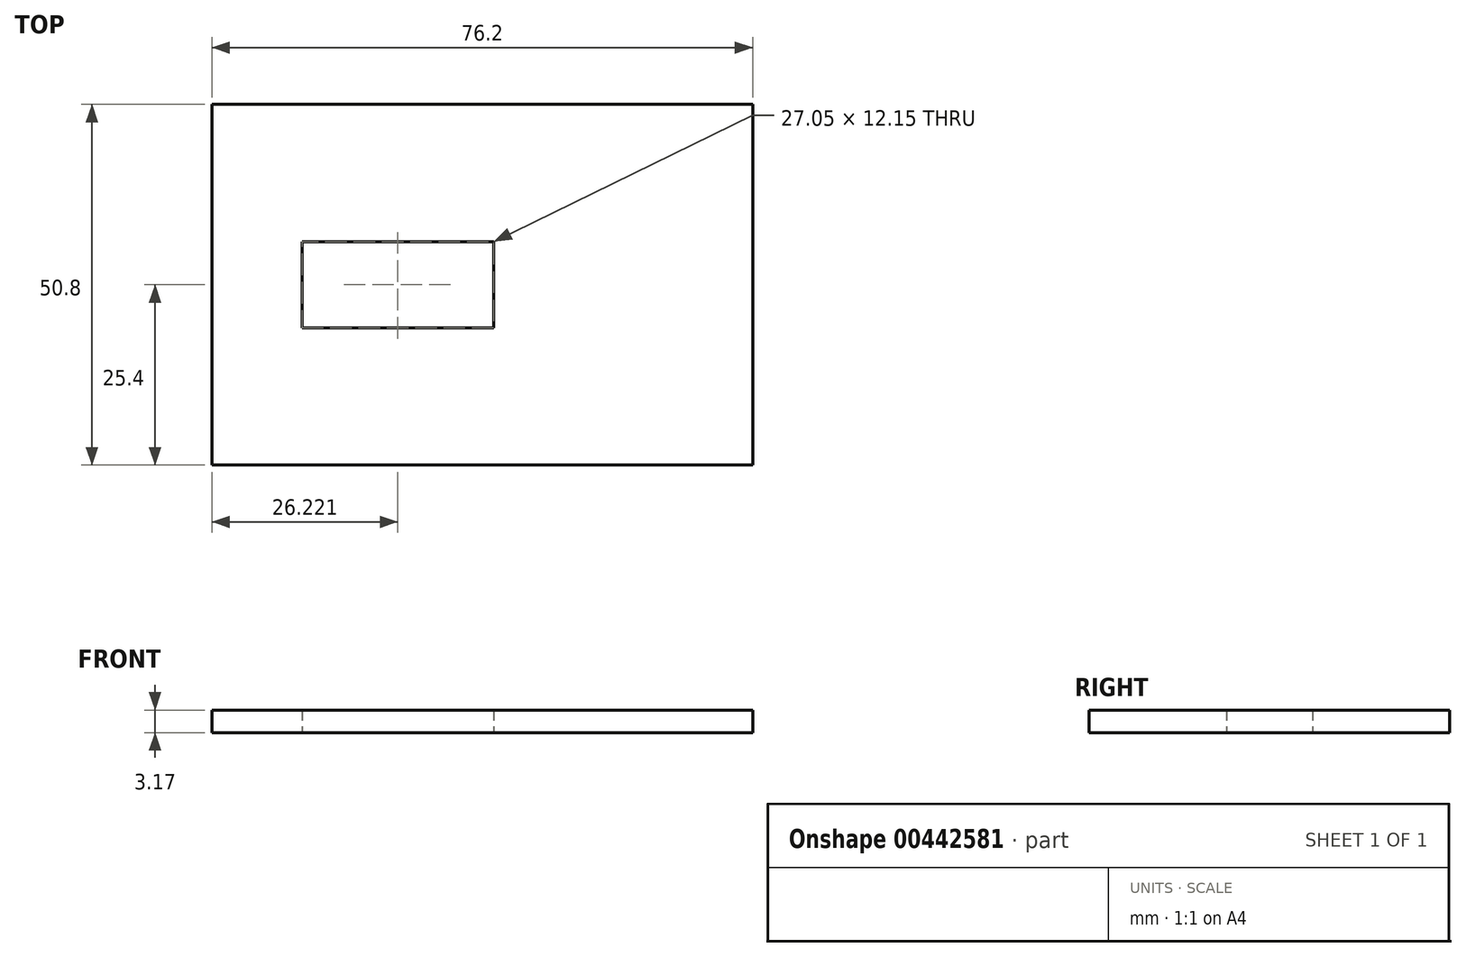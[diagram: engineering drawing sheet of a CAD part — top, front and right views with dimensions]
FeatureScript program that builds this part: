
annotation { "Feature Type Name" : "Feature", "Feature Type Description" : "" }
export const myFeature = defineFeature(function(context is Context, id is Id, definition is map)
    precondition{}
    {
        {
            var Q0;
            Q0=qCreatedBy(makeId("Top.planeOp"),FACE);
            var sketch = newSketch(context, id + "F0", { "sketchPlane" : qUnion([Q0])});
            skLineSegment(sketch, "E0.bottom", {"start": v(-39.23, -25.4) * mm, "end": v(36.97, -25.4) * mm});
            skLineSegment(sketch, "E0.top", {"start": v(-39.23, 25.4) * mm, "end": v(36.97, 25.4) * mm});
            skLineSegment(sketch, "E0.left", {"start": v(-39.23, -25.4) * mm, "end": v(-39.23, 25.4) * mm});
            skLineSegment(sketch, "E0.right", {"start": v(36.97, -25.4) * mm, "end": v(36.97, 25.4) * mm});
            skPoint(sketch, "E1", {"position": v(-39.23, 0) * mm});
            skPoint(sketch, "E2", {"position": v(36.97, 0) * mm});
            skLineSegment(sketch, "E3.bottom", {"start": v(-26.53, 6.08) * mm, "end": v(0.51, 6.08) * mm});
            skLineSegment(sketch, "E3.top", {"start": v(-26.53, -6.08) * mm, "end": v(0.51, -6.08) * mm});
            skLineSegment(sketch, "E3.left", {"start": v(-26.53, 6.08) * mm, "end": v(-26.53, -6.08) * mm});
            skLineSegment(sketch, "E3.right", {"start": v(0.51, 6.08) * mm, "end": v(0.51, -6.08) * mm});
            skPoint(sketch, "E4", {"position": v(0, 0) * mm});
            skPoint(sketch, "E5", {"position": v(-26.53, 0) * mm});
            skPoint(sketch, "E6", {"position": v(0.51, 0) * mm});
            skLineSegment(sketch, "E7", {"start": v(-39.23, 0) * mm, "end": v(-26.53, 0) * mm});
            skSolve(sketch);
        }
        {
            var Q0;
            Q0=makeQuery(id+"F0.imprint","IMPRINT",FACE,{"disambiguationData":[TD([[makeQuery(id+"F0.imprint","IMPRINT",EDGE,{"derivedFrom":sQuery(id+"F0.wireOp",EDGE,"E0.bottom")}),1.0]])]});
            extrude(context, id + "F1", {"entities" : qUnion([Q0]), "depth" : 3.17 * mm});
        }
    });
